# Revit family: Stirnplatte 45 quer
name_source: partatom
category: HLS-Bauteile
revit_build: Autodesk Revit 2017 (Build: 20190507_1515(x64)
units: mm (PartAtom-declared; Revit-internal decimal feet)

## family parameters
Basisbauteil = Fläche
Beim Laden mit Abzugskörper schneiden = Nein
Bemaßung runder Anschluss = Durchmesser verwenden
Gemeinsam genutzt = Ja
Raumberechnungspunkt = Nein
Teiletyp = Normal

## types (1)
- Stirnplatte 45 quer
    Anzugsmoment (M12) = 0.00 kip-ft
    Artikelnummer = 081646501
    Breite Schenkel = 0 mm  [stored 0 ft]
    EAN = 4250928447999
    Fabrikat = MEFA
    Firma = MEFA Befestigungs- und Montagesysteme GmbH
    Gewicht = 0.49 kg
    Gewicht pro Bauteil = 0.49 kg
    Kurztext1 = Stirnplatte C-Profil 45 quer
    Kurztext2 = für C-Profil 45/45 gvz
    Lochdurchmesser = 13,5 mm
    Länge Schenkel = 0 mm  [stored 0 ft]
    Material = Stahl
    Mengeneinheit = St
    Oberflaeche = galvanisch verzinkt
    Profil = C-Profil
    Profiltyp = 45/45
    Stärke Material = 0 mm  [stored 0 ft]
    Vorgabe-Ansicht = 1219 mm
    max. zul. Last mit Profil = 0.00 kip
    max. zul. Last ohne Profil = 0.00 kip
    vpe = 25 St

note: [stored X ft] marks values corroborated as IEEE doubles in the binary element streams (Revit-internal decimal feet)
